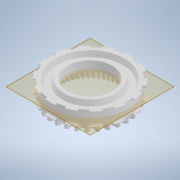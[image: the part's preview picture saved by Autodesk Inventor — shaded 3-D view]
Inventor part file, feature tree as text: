
AUTODESK INVENTOR PART (.ipt)
format: ipt  version: 2022 (Build 260153000, 153)  size: 1,679,872 bytes
history: native  units: mm
features: extrude x9, sketch x9, projected_geometry x8, other x7, pattern_circular x3, chamfer x2, revolve x1, fillet x1, mirror x1, reference x1
ambient origin geometry x8: Origin, YZ Plane, XZ Plane, XY Plane, X Axis, Y Axis, Z Axis, Center Point
bodies: Body1 (feature_tree)
feature tree (42):
  other  "Твердое тело1"
  extrude  "Выдавливание1"  Depth=70.0mm
  extrude  "Выдавливание2"  Depth=3.0mm
  extrude  "Выдавливание3"  Depth=37.0mm
  extrude  "Выдавливание4"  Depth=25.25mm
  pattern_circular  "Круговой массив1"  [2 undecoded]
  revolve  "Вращение1"
  fillet  "Сопряжение1"  Radius=12.0mm
  other  "РабПлоскость1"
  mirror  "Зеркальное отражение1"
  extrude  "Выдавливание5"  Depth=13.0mm
  pattern_circular  "Круговой массив2"  [2 undecoded]
  extrude  "Выдавливание6"  Depth=2.0mm
  other  "НаклГрань1"
  other  "НаклГрань2"
  extrude  "Выдавливание7"  Depth=4.8mm TaperAngle=0.0deg
  extrude  "Выдавливание8"  Depth=5.0mm TaperAngle=0.0deg
  chamfer  "Фаска1"  Distance=500.0mm Angle=360.0deg
  pattern_circular  "Круговой массив3"  [2 undecoded]
  extrude  "Выдавливание9"  Depth=0.8mm
  chamfer  "Фаска2"  Distance=3.0mm
  sketch  "Эскиз1"
  sketch  "Эскиз2"
  projected_geometry  "Спроецированная петля1"
  reference  "Ссылка1"
  sketch  "Эскиз3"
  projected_geometry  "Спроецированная петля2"
  projected_geometry  "Спроецированная петля3"
  sketch  "Эскиз5"
  projected_geometry  "Спроецированная петля4"
  sketch  "Эскиз6"
  projected_geometry  "Спроецированная петля5"
  sketch  "Эскиз7"
  projected_geometry  "Спроецированная петля6"
  sketch  "Эскиз8"
  projected_geometry  "Спроецированная петля7"
  sketch  "Эскиз10"
  sketch  "Эскиз11"
  projected_geometry  "Спроецированная петля8"
  other  "<userpath>\Documents\Git\MZCAT_2024\MZCAT.iam"
  other  "MZCAT.iam"
  other  "motor:2"
note: 6 required parameter values undecoded (feature->parameter linkage not recoverable at this tier; creation-order binding heuristic only, values carry confidence <= 0.55)
